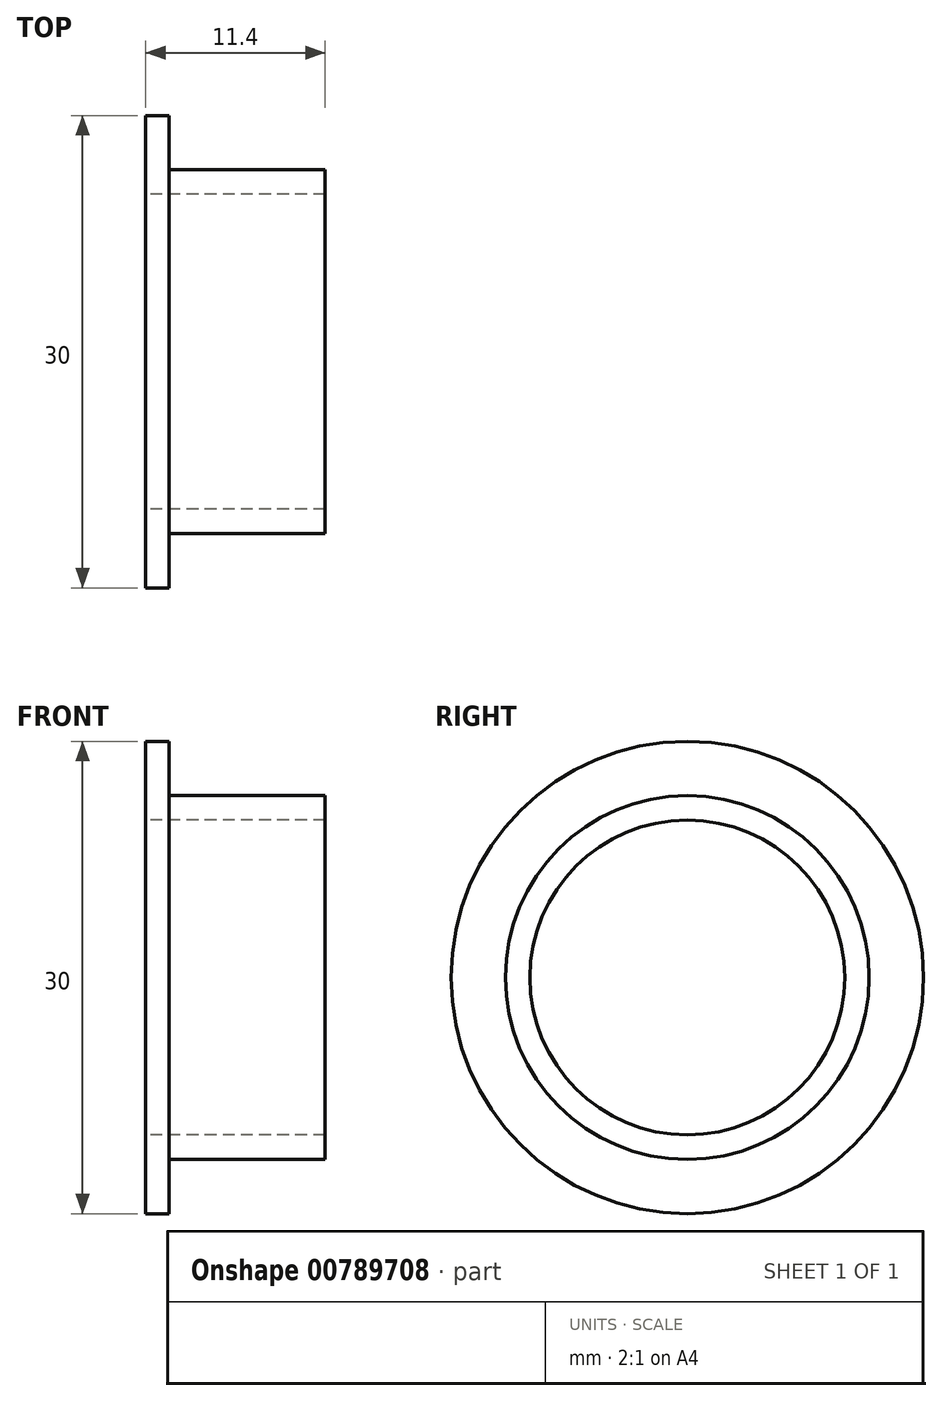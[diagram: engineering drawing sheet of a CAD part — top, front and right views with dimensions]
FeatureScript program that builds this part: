
annotation { "Feature Type Name" : "Feature", "Feature Type Description" : "" }
export const myFeature = defineFeature(function(context is Context, id is Id, definition is map)
    precondition{}
    {
        {
            var Q0;
            Q0=qCreatedBy(makeId("Front.planeOp"),FACE);
            var sketch = newSketch(context, id + "F0", { "sketchPlane" : qUnion([Q0])});
            skLineSegment(sketch, "E0", {"start": v(0, 0) * mm, "end": v(35.67, 0) * mm, "construction": true});
            skLineSegment(sketch, "E1", {"start": v(0, 10) * mm, "end": v(0, 15) * mm});
            skLineSegment(sketch, "E2", {"start": v(0, 15) * mm, "end": v(1.5, 15) * mm});
            skLineSegment(sketch, "E3", {"start": v(1.5, 15) * mm, "end": v(1.5, 11.55) * mm});
            skLineSegment(sketch, "E4", {"start": v(1.5, 11.55) * mm, "end": v(11.4, 11.55) * mm});
            skLineSegment(sketch, "E5", {"start": v(11.4, 11.55) * mm, "end": v(11.4, 10) * mm});
            skLineSegment(sketch, "E6", {"start": v(11.4, 10) * mm, "end": v(0, 10) * mm});
            skSolve(sketch);
        }
        {
            var Q0;
            Q0 = qSketchRegion(id + "F0", true);
            var Q1;
            Q1=sQuery(id+"F0.wireOp",EDGE,"E0");
            revolve(context, id + "F1", {"surfaceOperationType" : NewSurfaceOperationType.NEW, "entities" : qUnion([Q0]), "axis" : qUnion([Q1]), "revolveType" : RevolveType.FULL});
        }
    });
